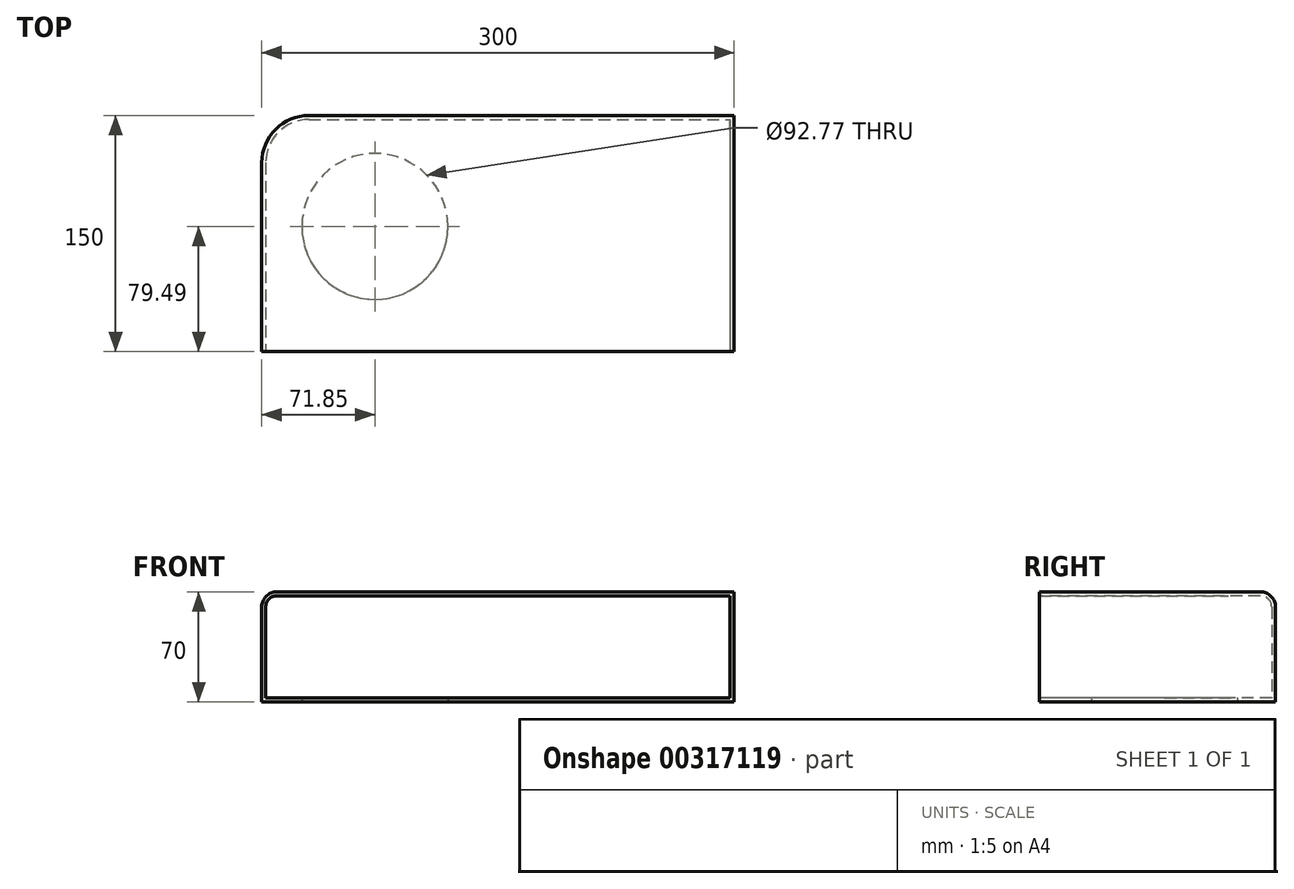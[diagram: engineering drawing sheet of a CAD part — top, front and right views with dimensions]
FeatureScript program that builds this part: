
annotation { "Feature Type Name" : "Feature", "Feature Type Description" : "" }
export const myFeature = defineFeature(function(context is Context, id is Id, definition is map)
    precondition{}
    {
        {
            var Q0;
            Q0=qCreatedBy(makeId("Top.planeOp"),FACE);
            var sketch = newSketch(context, id + "F0", { "sketchPlane" : qUnion([Q0])});
            skLineSegment(sketch, "E0.bottom", {"start": v(-148.65, 70.51) * mm, "end": v(151.35, 70.51) * mm});
            skLineSegment(sketch, "E0.top", {"start": v(-148.65, -79.49) * mm, "end": v(151.35, -79.49) * mm});
            skLineSegment(sketch, "E0.left", {"start": v(-148.65, 70.51) * mm, "end": v(-148.65, -79.49) * mm});
            skLineSegment(sketch, "E0.right", {"start": v(151.35, 70.51) * mm, "end": v(151.35, -79.49) * mm});
            skSolve(sketch);
        }
        {
            var Q0;
            Q0 = qSketchRegion(id + "F0", true);
            extrude(context, id + "F1", {"entities" : qUnion([Q0]), "endBound" : BoundingType.SYMMETRIC, "oppositeDirection" : true, "depth" : 70 * mm});
        }
        {
            var Q0;
            Q0=makeQuery(id+"F1.opExtrude","SWEPT_EDGE",EDGE,{"disambiguationData":[OSD([sQuery(id+"F0.wireOp",EDGE,"E0.bottom"),sQuery(id+"F0.wireOp",EDGE,"E0.left")])]});
            fillet(context, id + "F2", {"entities" : qUnion([Q0]), "radius" : 30 * mm, "tangentPropagation" : true, "allowEdgeOverflow" : false});
        }
        {
            var Q0;
            Q0=makeQuery(id+"F1.opExtrude","CAP_EDGE",EDGE,{"disambiguationData":[OSD([sQuery(id+"F0.wireOp",EDGE,"E0.bottom")])],"isStart":true});
            fillet(context, id + "F3", {"entities" : qUnion([Q0]), "radius" : 9.66 * mm, "tangentPropagation" : true, "allowEdgeOverflow" : false});
        }
        {
            var Q0;
            Q0=makeQuery(id+"F1.opExtrude","SWEPT_FACE",FACE,{"disambiguationData":[OSD([sQuery(id+"F0.wireOp",EDGE,"E0.top")])]});
            shell(context, id + "F4", {"entities" : qUnion([Q0]), "thickness" : 2.5 * mm});
        }
        {
            var Q0;
            Q0=makeQuery(id+"F1.opExtrude","CAP_FACE",FACE,{"disambiguationData":[OSD([sQuery(id+"F0.wireOp",EDGE,"E0.bottom"),sQuery(id+"F0.wireOp",EDGE,"E0.top"),sQuery(id+"F0.wireOp",EDGE,"E0.left"),sQuery(id+"F0.wireOp",EDGE,"E0.right")])],"isStart":false});
            var sketch = newSketch(context, id + "F5", { "sketchPlane" : qUnion([Q0])});
            skCircle(sketch, "E1", {"center": v(-76.8, 0) * mm, "radius": 46.38 * mm});
            skSolve(sketch);
        }
        {
            var Q0;
            Q0 = qSketchRegion(id + "F5", true);
            extrude(context, id + "F6", {"entities" : qUnion([Q0]), "operationType" : NewBodyOperationType.REMOVE, "oppositeDirection" : true, "depth" : 14 * mm});
        }
    });
